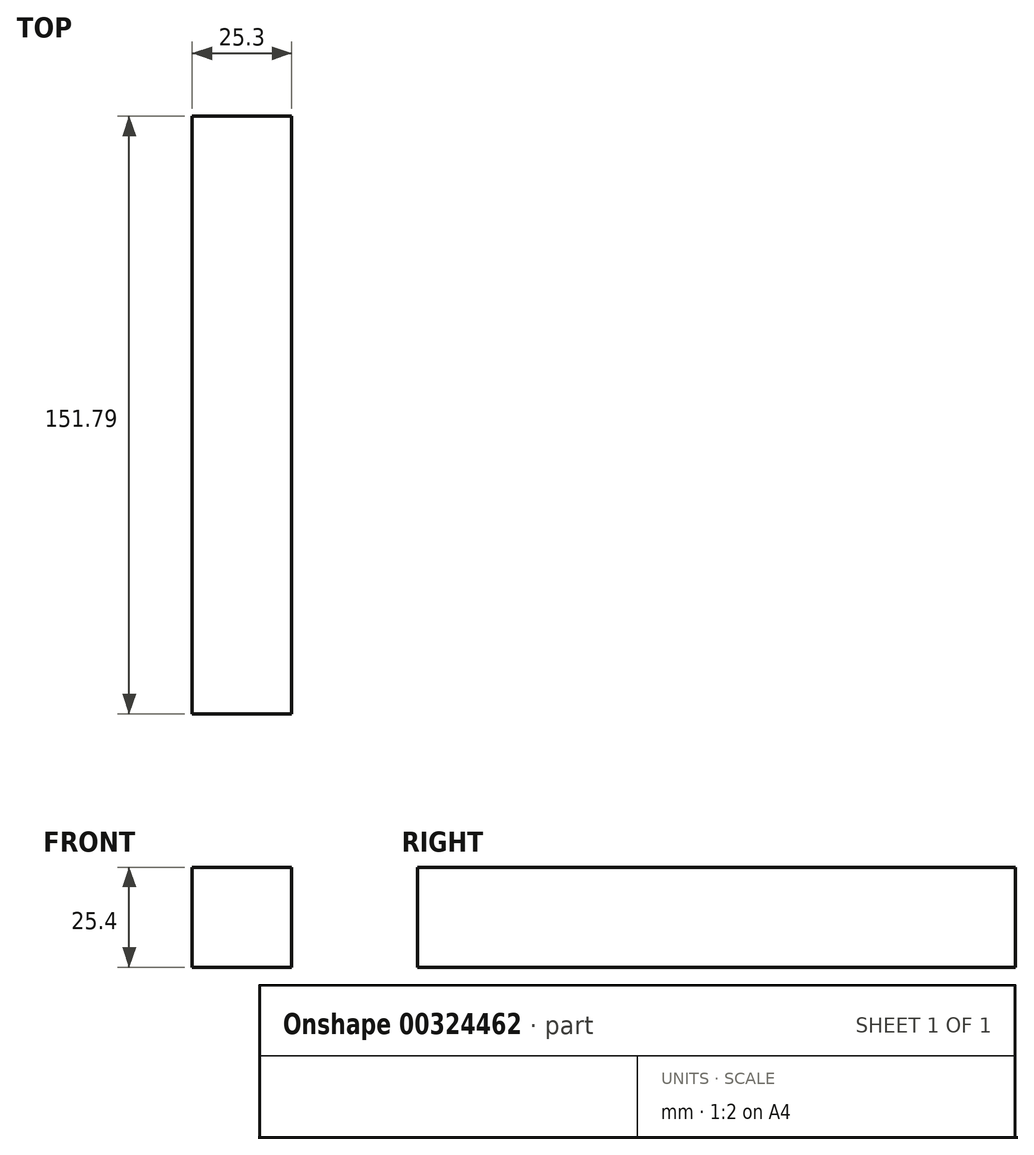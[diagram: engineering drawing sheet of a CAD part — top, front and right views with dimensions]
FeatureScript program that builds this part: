
annotation { "Feature Type Name" : "Feature", "Feature Type Description" : "" }
export const myFeature = defineFeature(function(context is Context, id is Id, definition is map)
    precondition{}
    {
        {
            var Q0;
            Q0=qCreatedBy(makeId("Top.planeOp"),FACE);
            var sketch = newSketch(context, id + "F0", { "sketchPlane" : qUnion([Q0])});
            skLineSegment(sketch, "E0.bottom", {"start": v(-75.6, 76.05) * mm, "end": v(-50.3, 76.05) * mm});
            skLineSegment(sketch, "E0.top", {"start": v(-75.6, -75.74) * mm, "end": v(-50.3, -75.74) * mm});
            skLineSegment(sketch, "E0.left", {"start": v(-75.6, 76.05) * mm, "end": v(-75.6, -75.74) * mm});
            skLineSegment(sketch, "E0.right", {"start": v(-50.3, 76.05) * mm, "end": v(-50.3, -75.74) * mm});
            skSolve(sketch);
        }
        {
            var Q0;
            Q0 = qSketchRegion(id + "F0", true);
            extrude(context, id + "F1", {"entities" : qUnion([Q0]), "depth" : 25.4 * mm});
        }
    });
